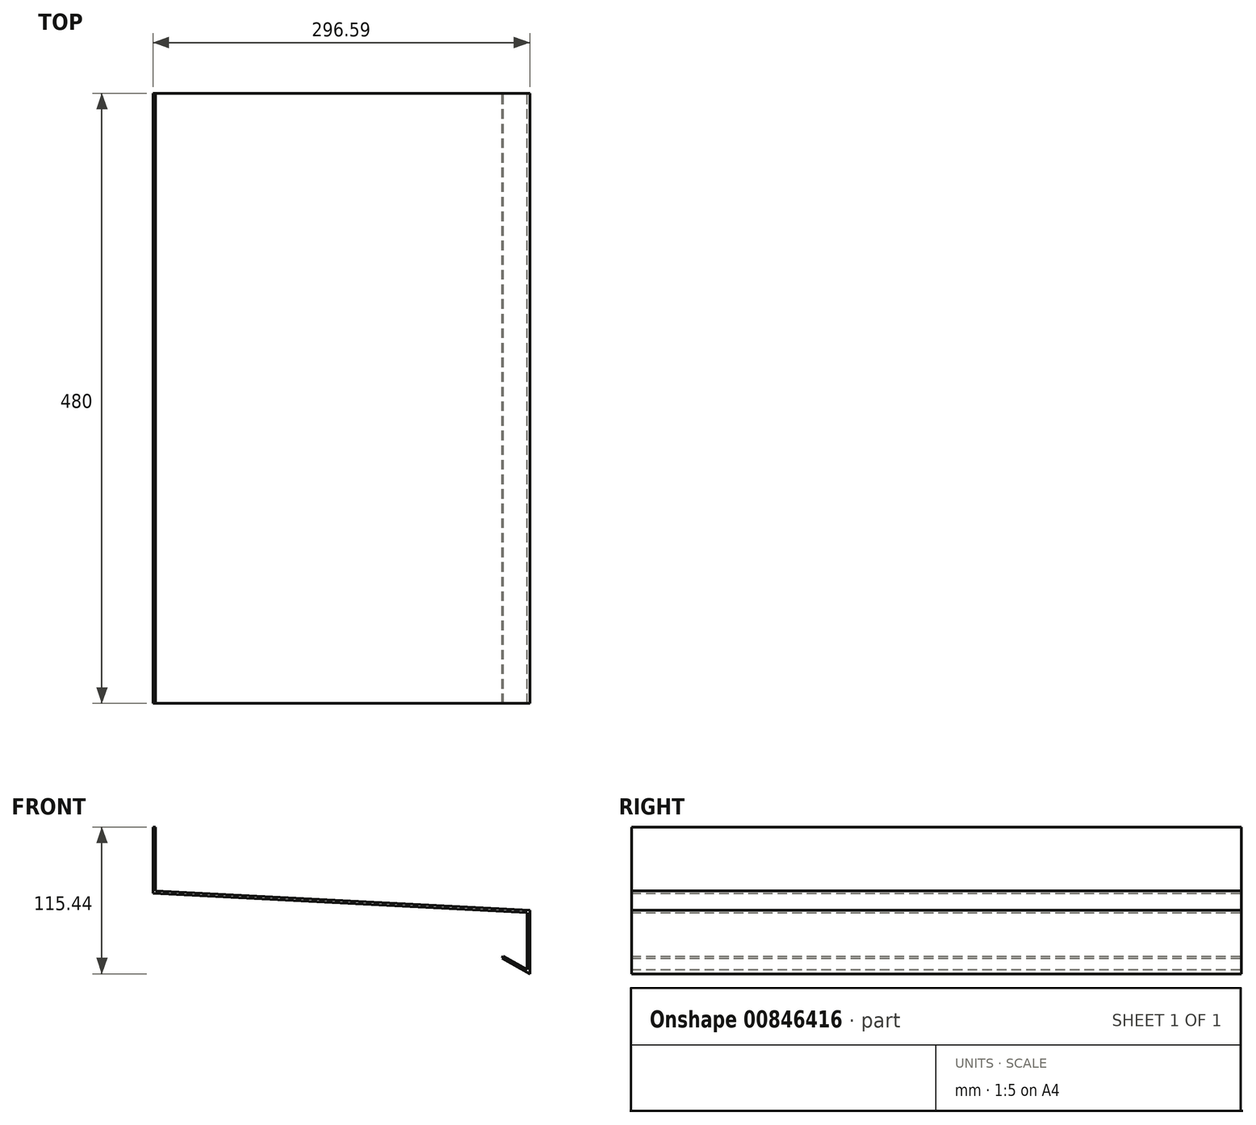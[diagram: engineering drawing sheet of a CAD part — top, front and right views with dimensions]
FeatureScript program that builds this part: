
annotation { "Feature Type Name" : "Feature", "Feature Type Description" : "" }
export const myFeature = defineFeature(function(context is Context, id is Id, definition is map)
    precondition{}
    {
        {
            var Q0;
            Q0=qCreatedBy(makeId("Front.planeOp"),FACE);
            var sketch = newSketch(context, id + "F0", { "sketchPlane" : qUnion([Q0])});
            skLineSegment(sketch, "E0", {"start": v(-16.73, 16.98) * mm, "end": v(-14.73, 16.98) * mm});
            skLineSegment(sketch, "E1", {"start": v(-14.73, 16.98) * mm, "end": v(-14.73, -33.02) * mm});
            skLineSegment(sketch, "E2", {"start": v(-14.73, -33.02) * mm, "end": v(279.86, -48.46) * mm});
            skLineSegment(sketch, "E3", {"start": v(279.86, -48.46) * mm, "end": v(279.86, -98.46) * mm});
            skLineSegment(sketch, "E4", {"start": v(279.86, -98.46) * mm, "end": v(258.05, -86.24) * mm});
            skLineSegment(sketch, "E5", {"start": v(-16.73, 16.98) * mm, "end": v(-16.73, -35.02) * mm});
            skLineSegment(sketch, "E6", {"start": v(-16.73, -35.02) * mm, "end": v(277.86, -50.46) * mm});
            skLineSegment(sketch, "E7", {"start": v(277.86, -50.46) * mm, "end": v(277.86, -95.05) * mm});
            skLineSegment(sketch, "E8", {"start": v(259.03, -84.5) * mm, "end": v(258.05, -86.24) * mm});
            skLineSegment(sketch, "E9.trimOffspring", {"start": v(277.86, -95.05) * mm, "end": v(259.03, -84.5) * mm});
            skSolve(sketch);
        }
        {
            var Q0;
            Q0 = qSketchRegion(id + "F0", true);
            extrude(context, id + "F1", {"entities" : qUnion([Q0]), "depth" : 480 * mm, "offsetDistance" : 25 * mm});
        }
    });
